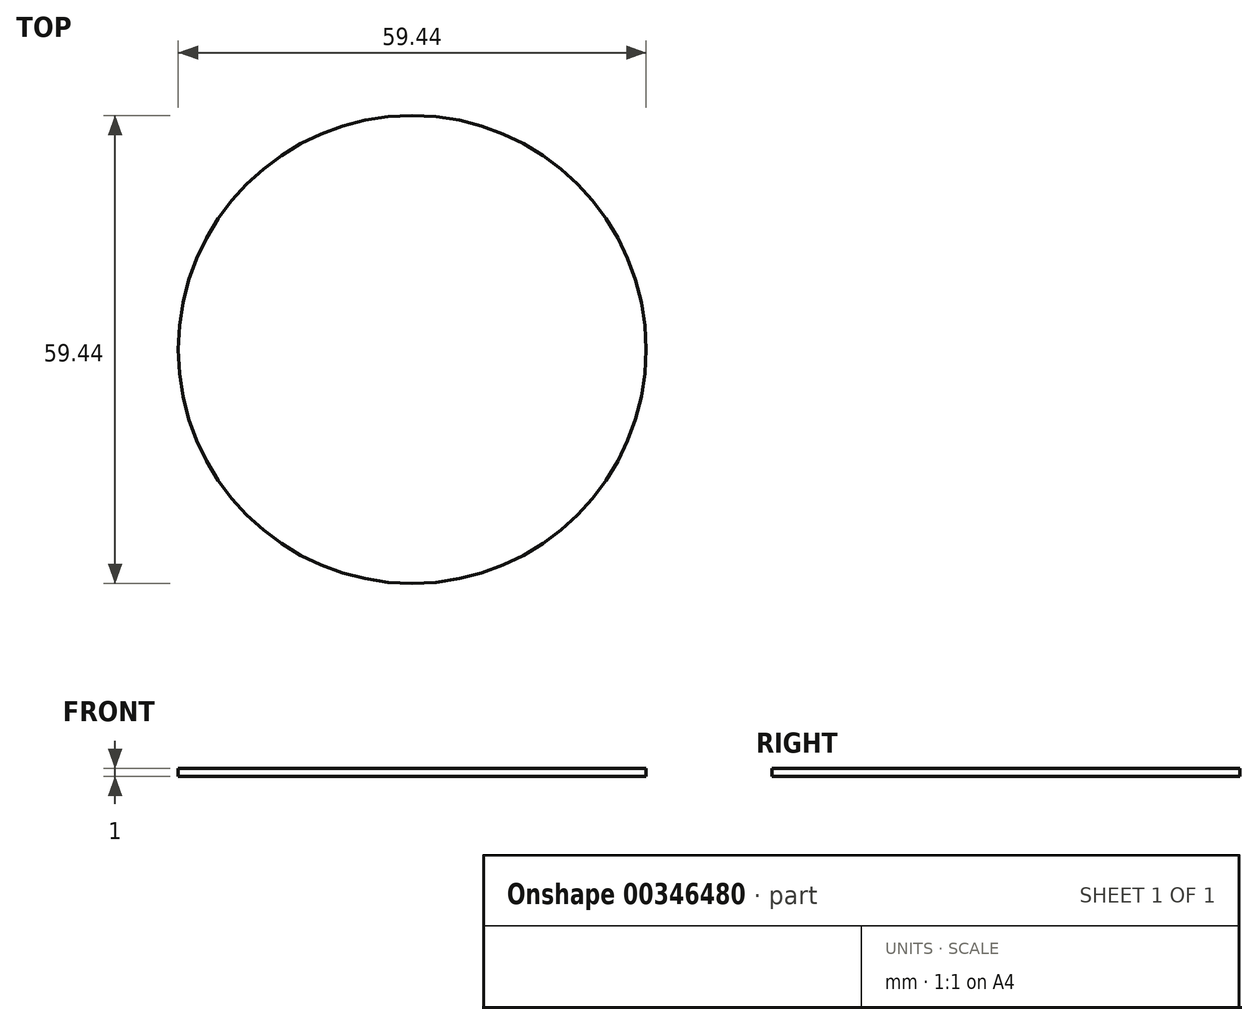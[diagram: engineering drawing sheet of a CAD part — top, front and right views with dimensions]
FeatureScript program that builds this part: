
annotation { "Feature Type Name" : "Feature", "Feature Type Description" : "" }
export const myFeature = defineFeature(function(context is Context, id is Id, definition is map)
    precondition{}
    {
        {
            var Q0;
            Q0=qCreatedBy(makeId("Top.planeOp"),FACE);
            var sketch = newSketch(context, id + "F0", { "sketchPlane" : qUnion([Q0])});
            skCircle(sketch, "E0", {"center": v(0, 0) * mm, "radius": 29.72 * mm});
            skSolve(sketch);
        }
        {
            var Q0;
            Q0 = qSketchRegion(id + "F0", true);
            extrude(context, id + "F1", {"entities" : qUnion([Q0]), "depth" : 1 * mm});
        }
    });
